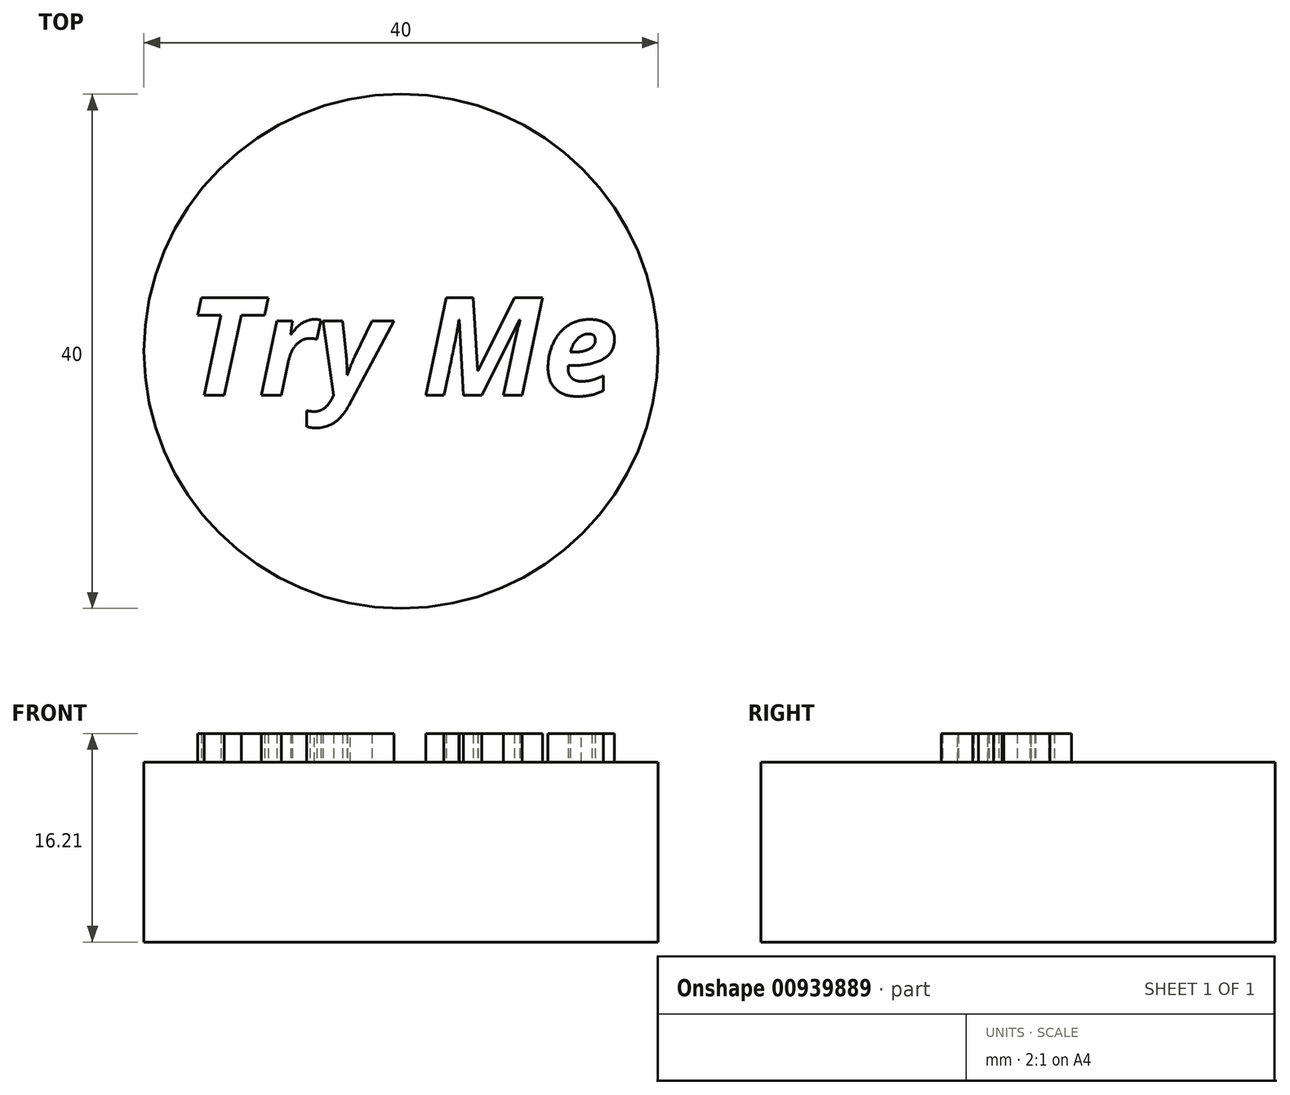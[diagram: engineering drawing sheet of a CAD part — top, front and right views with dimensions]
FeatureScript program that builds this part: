
annotation { "Feature Type Name" : "Feature", "Feature Type Description" : "" }
export const myFeature = defineFeature(function(context is Context, id is Id, definition is map)
    precondition{}
    {
        {
            var Q0;
            Q0=qCreatedBy(makeId("Top.planeOp"),FACE);
            var sketch = newSketch(context, id + "F0", { "sketchPlane" : qUnion([Q0])});
            skCircle(sketch, "E0", {"center": v(0, 0) * mm, "radius": 20 * mm});
            skSolve(sketch);
        }
        {
            var Q0;
            Q0=qSketchRegion(id+"F0",true);
            extrude(context, id + "F1", {"entities" : qUnion([Q0]), "depth" : 14 * mm, "offsetDistance" : 25.4 * mm});
        }
        {
            var Q0;
            Q0=makeQuery(id+"F1.opExtrude","CAP_FACE",FACE,{"disambiguationData":[OSD([sQuery(id+"F0.wireOp",EDGE,"E0")])],"isStart":false});
            var sketch = newSketch(context, id + "F2", { "sketchPlane" : qUnion([Q0])});
            skText(sketch, "E1", { "text": "Try Me", "fontName": "OpenSans-BoldItalic.ttf"});
            const initialGuessF2  = {"E1": [-0.0167, -0.00342, 1, 0, 0.00763]};
            skSetInitialGuess(sketch, initialGuessF2);
            skSolve(sketch);
        }
        {
            var Q0;
            Q0 = qSketchRegion(id + "F2", true);
            extrude(context, id + "F3", {"entities" : qUnion([Q0]), "operationType" : NewBodyOperationType.ADD, "depth" : 2.2 * mm, "offsetDistance" : 25.4 * mm});
        }
    });
